# Revit family: LFX_A3-M-Troffer-Lens
name_source: partatom
category: Lighting Fixtures
revit_build: Autodesk Revit 2016 (Build: 20150220_1215(x64)
units: mm (PartAtom-declared; Revit-internal decimal feet)

## family parameters
Always vertical = Yes
Cut with Voids When Loaded = No
Host = Ceiling
Light Source = Yes
Part Type = Normal
Room Calculation Point = No
Round Connector Dimension = Use Diameter
Shared = No

## types (6) — shared parameters
Color Filter = 16777215
Diffuser = Glass - White, High Luminance
Dimming Lamp Color Temperature Shift = <None>
Emit from Line Length = 1149 mm
Lamp = T-12
Light Box = Metal - Chrome
Light Source Symbol Size = 610 mm

## per-type parameters (varying)
| type | Circle Diameter | Length | Wattage Comments | Width |
| 0300 x 1200mm (2 Lamp) | 180 mm | 1200 mm  [stored 3.93701 ft] | (2)20 | 300 mm |
| 0600 x 0600mm (4 Lamp) | 360 mm  [stored 1.1811 ft] | 600 mm | (4)20 | 600 mm |
| 0600 x 1200mm (2 Lamps) | 360 mm  [stored 1.1811 ft] | 1200 mm  [stored 3.93701 ft] | (2)20 | 600 mm |
| 0600 x 1200mm (4 Lamps) | 360 mm  [stored 1.1811 ft] | 1200 mm  [stored 3.93701 ft] | (4)20 | 600 mm |
| 0600 x 0600mm (2 Lamp) | 360 mm  [stored 1.1811 ft] | 600 mm | (4)20 | 600 mm |
| Ceiling Lens | 360 mm  [stored 1.1811 ft] | 1200 mm  [stored 3.93701 ft] | (2)20 | 600 mm |

note: [stored X ft] marks values corroborated as IEEE doubles in the binary element streams (Revit-internal decimal feet)

## geometry (parser evidence)
native form markers: Sweep x1
no freeform markers — native parametric forms only
